# Revit family: RFADBX18
name_source: partatom
category: Generic Models
revit_build: Autodesk Revit MEP 2013 (Build: 20130531_2115(x64)
units: mm (PartAtom-declared; Revit-internal decimal feet)

## types (1)
- DBX_Electronically Controlled Instantaneous Water Heaters
    7 day Electronic Programming = No
    BMS Links = No
    Backflow Prevention Valve = Not fitted
    Button Interface = Yes
    Cable Length and size (If Fitted) = Not fitted
    Control Thermostat Range = 30°C-60°C
    Enclosure Rating = IP25
    External Material = High impact resistant white plastic
    Gross Weight = 3.7kg
    Internal Filter (if fitted) = Not Fitted
    Mains Pressure Limiting Valve = Not Fitted
    Mains Water Connection = 1/2” BSP
    Mains Water Pressure (Maximum) = The appliance must not be subject to more than 1.0 MPa (10 bar).
    Mains Water Pressure (Minimum) = 0.2 MPa (2 bar) is recommended for optimum performance.
    Manufacturer = Zip Industries(UK) Ltd
    Model = DBX18
    Net Weight = 3.3kg
    Overall Height = 540
    Overall Length/Depth = 160
    Overall Width = 295
    Power Rating = 18.0
    Power Supply (Voltage) = PE 380-400
    Product Range = Instantaneous Water Heaters
    Programmable Function Parameters = YES
    Programmable Safety Features = YES
    Shape = Rectangular
    Shipping Weight = Not Known
    Standby Power Loss (idle mode) = Not Known
    Supply Phase = 3
    Touch Screen Control Panel = Yes
    Type Comments = Boiling Water Heater (Potable)
    Type/Usage = Wall mounted
    URL = www.zipindustries.co.uk
    WRAS Approved = Yes
    Warranty ID = 12 months
    l Flow Rate @ 50°C(3)  l/m = 9.8(4)

## geometry (parser evidence)
native form markers: Sweep x1
no freeform markers — native parametric forms only
